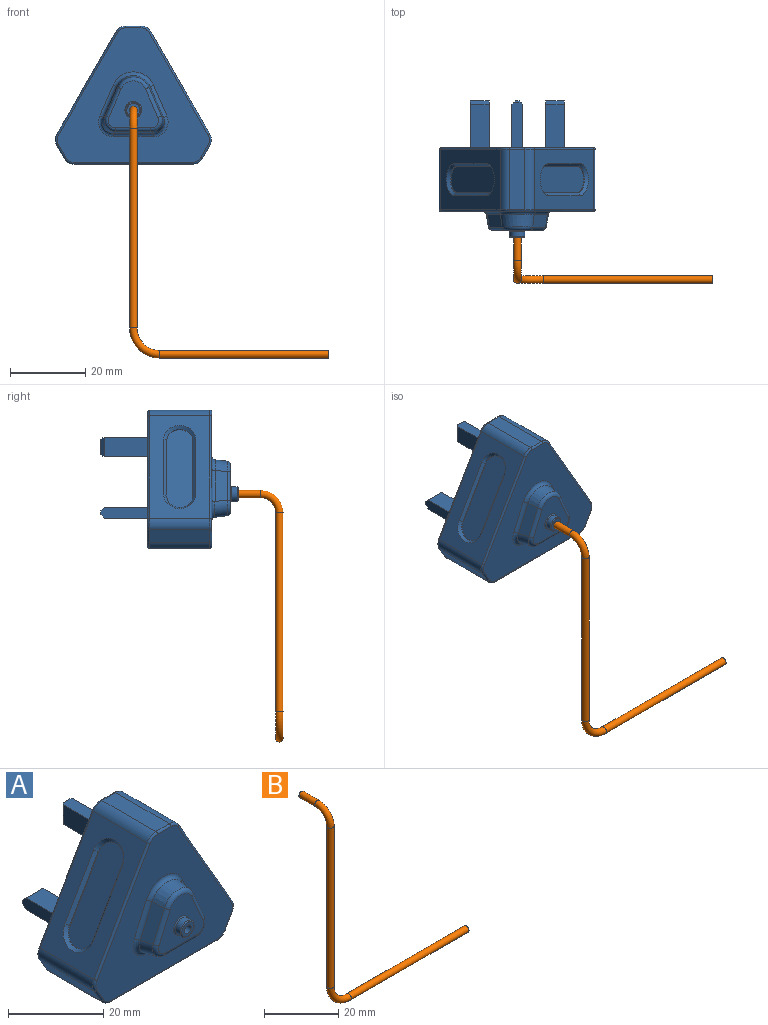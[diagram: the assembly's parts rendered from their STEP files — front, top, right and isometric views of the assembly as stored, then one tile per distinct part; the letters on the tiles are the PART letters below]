
ASSEMBLY  parts=2 mates=1
PART A: 104 faces, bbox 42.1x36.5x37.3 mm
  f0: plane 27.31x16mm, normal (0.87,0,0.5), area 303.3mm2, adj f33,f34,f43,f61,f100,f101,f102,f103
  f1: plane 27.31x16mm, normal (-0.87,0,0.5), area 303.3mm2, adj f35,f36,f42,f56,f91,f92,f93,f94
  f2: plane 31.54x16mm, normal (0,0,-1), area 504.6mm2, adj f37,f38,f50,f53
  f3: plane 40.57x35.81mm, normal (0,-1,0), area 703.5mm2, adj f22,f23,f24,f25,f26,f27,f39,f40
  f4: plane 40.57x35.81mm, normal (0,1,0), area 899.6mm2, adj f51,f52,f53,f54,f55,f56,f57,f58
  f5: plane 8.19x3.91mm, normal (-0.91,-0.12,0.39), area 28.2mm2, adj f8,f14,f19,f26
  f6: plane 10.6x3.24mm, normal (0,-0.12,-0.99), area 32.7mm2, adj f14,f15,f20,f25
  f7: plane 8.19x3.91mm, normal (0.91,-0.12,0.39), area 28.2mm2, adj f8,f15,f16,f22
  f8: cone r=5mm half-angle=7deg, axis (0,1,0), area 35.7mm2, adj f5,f7,f17,f24
  f9: plane 13.37x12.52mm, normal (0,-1,0), area 103.5mm2, adj f16,f17,f18,f19,f20,f21,f28
  f10: cylinder r=1mm len=2mm, axis (0,1,0), area 12.6mm2, adj f12,f13
  f11: cylinder r=2mm len=4mm, axis (0,1,0), area 18.8mm2, adj f28,f29
  f12: plane 3.5x3.5mm, normal (0,-1,0), area 6.5mm2, adj f10,f29
  f13: plane 2x2mm, normal (0,-1,0), area 3.1mm2, adj f10
  f14: cylinder r=3mm len=4.61mm, axis (-0.18,0.98,-0.12), area 20.3mm2, adj f5,f6,f21,f27
  f15: cylinder r=3mm len=4.61mm, axis (0.18,0.98,-0.12), area 20.3mm2, adj f6,f7,f18,f23
  f16: cylinder r=1mm len=8.03mm, axis (0.4,0,-0.92), area 12mm2, adj f7,f9,f17,f18
  f17: torus R=3.5mm, axis (0,-1,0), area 13.8mm2, adj f8,f9,f16,f19
  f18: bspline ~4.16x2.97mm, area 7.1mm2, adj f9,f15,f16,f20
  f19: cylinder r=1mm len=8.03mm, axis (-0.4,0,-0.92), area 12mm2, adj f5,f9,f17,f21
  f20: cylinder r=1mm len=9.39mm, axis (1,0,0), area 13.6mm2, adj f6,f9,f18,f21
  f21: bspline ~4.16x2.97mm, area 7.1mm2, adj f9,f14,f19,f20
  f22: cylinder r=1mm len=8.58mm, axis (-0.4,0,0.92), area 12.9mm2, adj f3,f7,f23,f24
  f23: bspline ~5.55x3.98mm, area 9.3mm2, adj f3,f15,f22,f25
  f24: torus R=5.88mm, axis (0,-1,0), area 17.8mm2, adj f3,f8,f22,f26
  f25: cylinder r=1mm len=10.6mm, axis (-1,0,0), area 15.4mm2, adj f3,f6,f23,f27
  f26: cylinder r=1mm len=8.58mm, axis (0.4,0,0.92), area 12.9mm2, adj f3,f5,f24,f27
  f27: bspline ~5.55x3.98mm, area 9.3mm2, adj f3,f14,f25,f26
  f28: torus R=2.25mm, axis (0,-1,0), area 5.2mm2, adj f9,f11
  f29: torus R=1.75mm, axis (0,-1,0), area 4.7mm2, adj f11,f12
  f30: plane 16x3.5mm, normal (-0.87,0,-0.5), area 64.6mm2, adj f35,f37,f46,f52
  f31: plane 16x4.04mm, normal (0,0,1), area 64.6mm2, adj f33,f36,f39,f60
  f32: plane 16x3.5mm, normal (0.87,0,-0.5), area 64.6mm2, adj f34,f38,f47,f57
  f33: cylinder r=3mm len=16mm, axis (0,-1,0), area 50.3mm2, adj f0,f31,f41,f62
  f34: cylinder r=3mm len=16mm, axis (0,1,0), area 50.3mm2, adj f0,f32,f45,f59
  f35: cylinder r=3mm len=16mm, axis (0,-1,0), area 50.3mm2, adj f1,f30,f44,f54
  f36: cylinder r=3mm len=16mm, axis (0,1,0), area 50.3mm2, adj f1,f31,f40,f58
  f37: cylinder r=3mm len=16mm, axis (0,1,0), area 50.3mm2, adj f2,f30,f48,f51
  f38: cylinder r=3mm len=16mm, axis (0,-1,0), area 50.3mm2, adj f2,f32,f49,f55
  f39: cylinder r=0.5mm len=4.04mm, axis (1,0,0), area 3.2mm2, adj f3,f31,f40,f41
  f40: torus R=2.5mm, axis (0,-1,0), area 2.3mm2, adj f3,f36,f39,f42
  f41: torus R=2.5mm, axis (0,-1,0), area 2.3mm2, adj f3,f33,f39,f43
  f42: cylinder r=0.5mm len=27.56mm, axis (0.5,0,0.87), area 24.8mm2, adj f1,f3,f40,f44
  f43: cylinder r=0.5mm len=27.56mm, axis (0.5,0,-0.87), area 24.8mm2, adj f0,f3,f41,f45
  f44: torus R=2.5mm, axis (0,-1,0), area 2.3mm2, adj f3,f35,f42,f46
  f45: torus R=2.5mm, axis (0,-1,0), area 2.3mm2, adj f3,f34,f43,f47
  f46: cylinder r=0.5mm len=3.75mm, axis (-0.5,0,0.87), area 3.2mm2, adj f3,f30,f44,f48
  f47: cylinder r=0.5mm len=3.75mm, axis (-0.5,0,-0.87), area 3.2mm2, adj f3,f32,f45,f49
  f48: torus R=2.5mm, axis (0,-1,0), area 2.3mm2, adj f3,f37,f46,f50
  f49: torus R=2.5mm, axis (0,-1,0), area 2.3mm2, adj f3,f38,f47,f50
  f50: cylinder r=0.5mm len=31.54mm, axis (-1,0,0), area 24.8mm2, adj f2,f3,f48,f49
  f51: torus R=2.5mm, axis (0,-1,0), area 2.3mm2, adj f4,f37,f52,f53
  f52: cylinder r=0.5mm len=3.75mm, axis (-0.5,0,0.87), area 3.2mm2, adj f4,f30,f51,f54
  f53: cylinder r=0.5mm len=31.54mm, axis (1,0,0), area 24.8mm2, adj f2,f4,f51,f55
  f54: torus R=2.5mm, axis (0,-1,0), area 2.3mm2, adj f4,f35,f52,f56
  f55: torus R=2.5mm, axis (0,-1,0), area 2.3mm2, adj f4,f38,f53,f57
  f56: cylinder r=0.5mm len=27.56mm, axis (-0.5,0,-0.87), area 24.8mm2, adj f1,f4,f54,f58
  f57: cylinder r=0.5mm len=3.75mm, axis (-0.5,0,-0.87), area 3.2mm2, adj f4,f32,f55,f59
  f58: torus R=2.5mm, axis (0,-1,0), area 2.3mm2, adj f4,f36,f56,f60
  f59: torus R=2.5mm, axis (0,-1,0), area 2.3mm2, adj f4,f34,f57,f61
  f60: cylinder r=0.5mm len=4.04mm, axis (1,0,0), area 3.2mm2, adj f4,f31,f58,f62
  f61: cylinder r=0.5mm len=27.56mm, axis (-0.5,0,0.87), area 24.8mm2, adj f0,f4,f59,f62
  f62: torus R=2.5mm, axis (0,-1,0), area 2.3mm2, adj f4,f33,f60,f61
  f63: plane 12x3mm, normal (0,0,-1), area 35.8mm2, adj f4,f64,f66,f78,f79,f84
  f64: plane 11.5x5mm, normal (-1,0,0), area 57.5mm2, adj f4,f63,f65,f78
  f65: plane 12x3mm, normal (0,0,1), area 35.8mm2, adj f4,f64,f66,f78,f79,f85
  f66: plane 11.5x5mm, normal (1,0,0), area 57.5mm2, adj f4,f63,f65,f79
  f67: plane 4x1mm, normal (0,1,0), area 4mm2, adj f78,f79,f84,f85
  f68: plane 12.5x3mm, normal (-1,0,0), area 36.5mm2, adj f4,f69,f71,f72,f80,f81
  f69: plane 11.5x5mm, normal (0,0,1), area 57.5mm2, adj f4,f68,f70,f80
  f70: plane 12.5x3mm, normal (1,0,0), area 36.5mm2, adj f4,f69,f71,f72,f80,f81
  f71: plane 11.5x5mm, normal (0,0,-1), area 57.5mm2, adj f4,f68,f70,f81
  f72: plane 5x1mm, normal (0,1,0), area 5mm2, adj f68,f70,f80,f81
  f73: plane 11.5x5mm, normal (0,0,1), area 57.5mm2, adj f4,f74,f76,f83
  f74: plane 12.5x3mm, normal (1,0,0), area 36.5mm2, adj f4,f73,f75,f77,f82,f83
  f75: plane 11.5x5mm, normal (0,0,-1), area 57.5mm2, adj f4,f74,f76,f82
  f76: plane 12.5x3mm, normal (-1,0,0), area 36.5mm2, adj f4,f73,f75,f77,f82,f83
  f77: plane 5x1mm, normal (0,1,0), area 5mm2, adj f74,f76,f82,f83
  f78: plane 5x1mm, normal (-0.71,0.71,0), area 6.7mm2, adj f63,f64,f65,f67,f84,f85
  f79: plane 5x1mm, normal (0.71,0.71,0), area 6.7mm2, adj f63,f65,f66,f67,f84,f85
  f80: plane 5x1mm, normal (0,0.71,0.71), area 7.1mm2, adj f68,f69,f70,f72
  f81: plane 5x1mm, normal (0,0.71,-0.71), area 7.1mm2, adj f68,f70,f71,f72
  f82: plane 5x1mm, normal (0,0.71,-0.71), area 7.1mm2, adj f74,f75,f76,f77
  f83: plane 5x1mm, normal (0,0.71,0.71), area 7.1mm2, adj f73,f74,f76,f77
  f84: plane 2x0.5mm, normal (0,0.71,-0.71), area 1.1mm2, adj f63,f67,f78,f79
  f85: plane 2x0.5mm, normal (0,0.71,0.71), area 1.1mm2, adj f65,f67,f78,f79
  f86: plane 14.85x8.72mm, normal (0,1,0), area 4.2mm2, adj f87,f89,f90,f94
  f87: cylinder r=3.5mm len=7mm, axis (-0.87,0,0.5), area 2.7mm2, adj f86,f88,f90,f92
  f88: plane 14.85x8.72mm, normal (0,-1,0), area 4.2mm2, adj f87,f89,f90,f91
  f89: cylinder r=3.5mm len=7mm, axis (-0.87,0,0.5), area 2.7mm2, adj f86,f88,f90,f93
  f90: plane 20.78x12mm, normal (-0.87,0,0.5), area 157.5mm2, adj f86,f87,f88,f89
  f91: plane 15.1x9.15mm, normal (-0.61,-0.71,0.35), area 18mm2, adj f1,f88,f92,f93
  f92: cone r=4.25mm half-angle=45deg, axis (-0.87,0,0.5), area 12.9mm2, adj f1,f87,f91,f94
  f93: cone r=4.25mm half-angle=45deg, axis (-0.87,0,0.5), area 12.9mm2, adj f1,f89,f91,f94
  f94: plane 15.1x9.15mm, normal (-0.61,0.71,0.35), area 18mm2, adj f1,f86,f92,f93
  f95: plane 14.85x8.72mm, normal (0,1,0), area 4.2mm2, adj f96,f98,f99,f103
  f96: cylinder r=3.5mm len=7mm, axis (0.87,0,0.5), area 2.7mm2, adj f95,f97,f99,f102
  f97: plane 14.85x8.72mm, normal (0,-1,0), area 4.2mm2, adj f96,f98,f99,f100
  f98: cylinder r=3.5mm len=7mm, axis (0.87,0,0.5), area 2.7mm2, adj f95,f97,f99,f101
  f99: plane 20.78x12mm, normal (0.87,0,0.5), area 157.5mm2, adj f95,f96,f97,f98
  f100: plane 15.1x9.15mm, normal (0.61,-0.71,0.35), area 18mm2, adj f0,f97,f101,f102
  f101: cone r=3.5mm half-angle=45deg, axis (0.87,0,0.5), area 12.9mm2, adj f0,f98,f100,f103
  f102: cone r=3.5mm half-angle=45deg, axis (0.87,0,0.5), area 12.9mm2, adj f0,f96,f100,f103
  f103: plane 15.1x9.15mm, normal (0.61,0.71,0.35), area 18mm2, adj f0,f95,f101,f102
PART B: 7 faces, bbox 53.7x12.5x68.2 mm
  f0: plane 2x2mm, normal (0,1,0), area 3.1mm2, adj f2
  f1: plane 2x2mm, normal (1,0,0), area 3.1mm2, adj f6
  f2: cylinder r=1mm len=6mm, axis (0,-1,0), area 37.7mm2, adj f0,f3
  f3: torus R=5mm, axis (1,0,0), area 49.3mm2, adj f2,f4
  f4: cylinder r=1mm len=53mm, axis (0,0,-1), area 333mm2, adj f3,f5
  f5: torus R=7mm, axis (0,-1,0), area 69.1mm2, adj f4,f6
  f6: cylinder r=1mm len=45mm, axis (1,0,0), area 282.7mm2, adj f1,f5
PLACE A at identity fixed
PLACE B t=(0,-2,0)mm
MATE fastened A.f10 <-> B.f2  axis (0,-1,0) through (0,-24,0)mm
